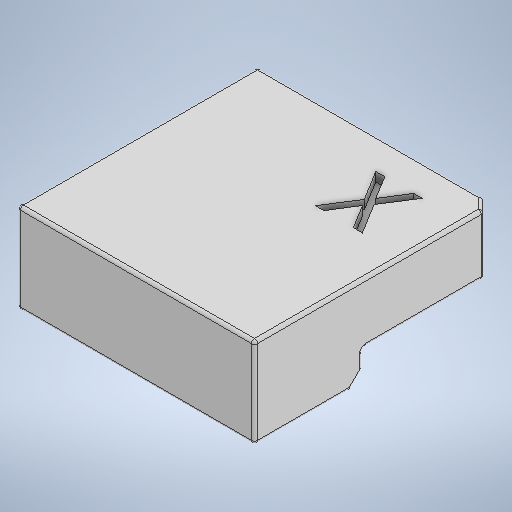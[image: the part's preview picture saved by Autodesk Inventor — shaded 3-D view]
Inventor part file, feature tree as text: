
AUTODESK INVENTOR PART (.ipt)
format: ipt  version: 2025 (Build 290162000, 162)  size: 269,824 bytes
history: native  units: mm
features: sketch x3, extrude x2, chamfer x2, emboss x1, fillet x1
ambient origin geometry x8: Origin, YZ Plane, XZ Plane, XY Plane, X Axis, Y Axis, Z Axis, Center Point
bodies: Solid1 (feature_tree)
feature tree (9):
  extrude  "Extrusion1"  Depth=40.1mm
  extrude  "Extrusion2"  Depth=2.0mm
  chamfer  "Chamfer1"  Distance=5.0mm
  chamfer  "Chamfer2"  Distance=2.0mm Angle=45.0deg
  emboss  "Emboss1"
  fillet  "Fillet1"  Radius=2.0mm
  sketch  "Sketch1"  dims[d0=39.6mm d1=40.1mm]
  sketch  "Sketch2"  dims[d2=15.0mm d3=0.0mm d4=2.0mm]
  sketch  "Sketch3"  dims[d5=2.0mm d6=5.0mm d7=0.0mm d8=2.0mm d9=2.0mm d10=45.0deg d11=2.0mm d12=2.0mm d13=45.0deg d14=1.5mm d15=0.0mm d16=0.5mm]
